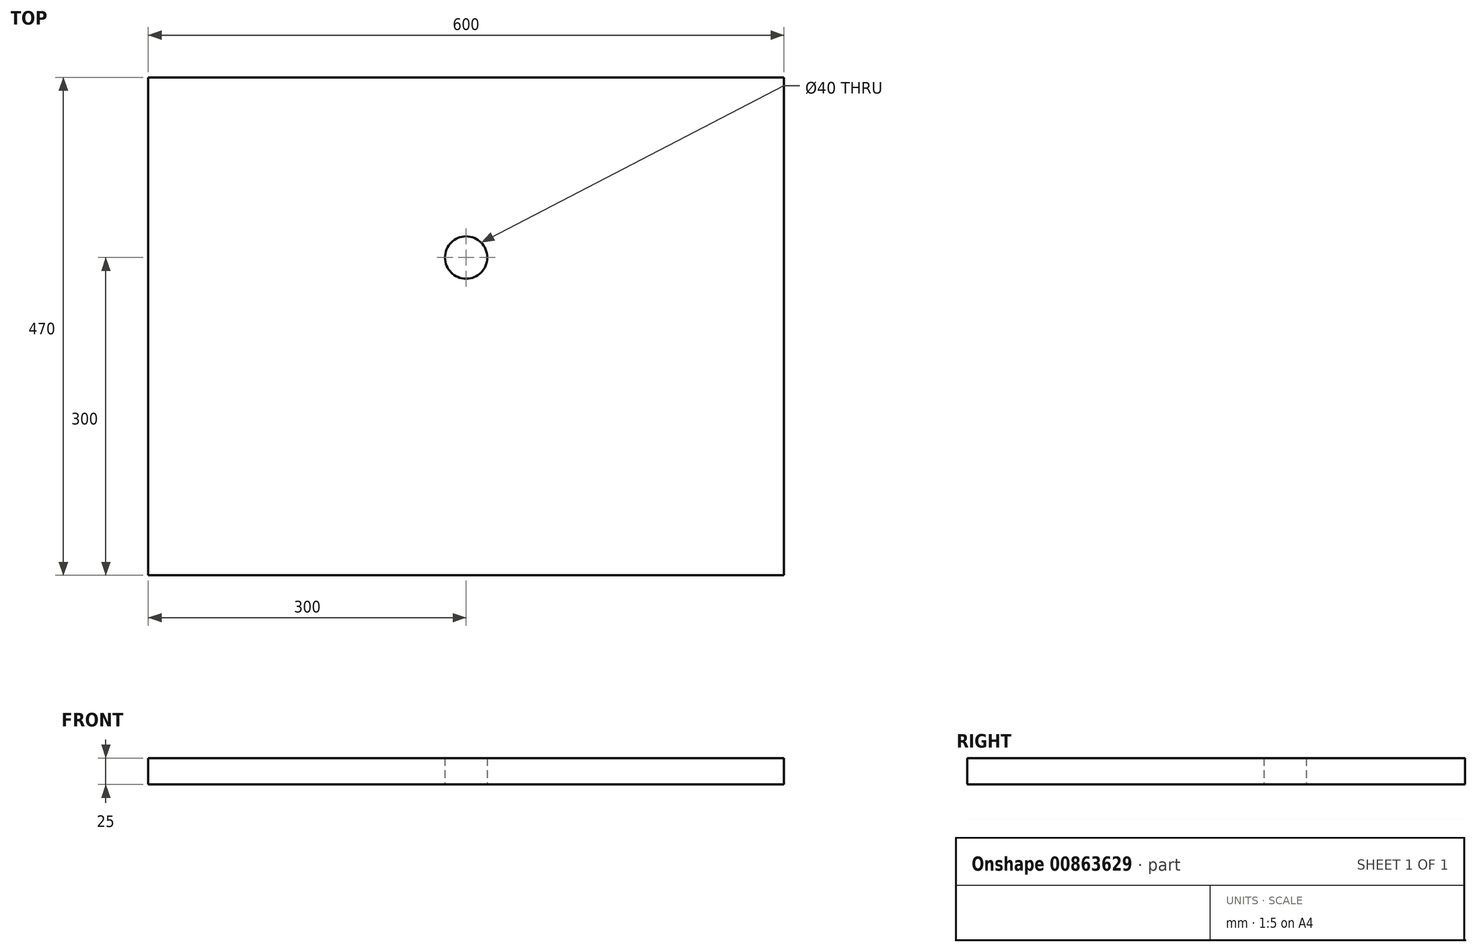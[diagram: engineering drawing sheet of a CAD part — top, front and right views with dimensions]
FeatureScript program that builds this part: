
annotation { "Feature Type Name" : "Feature", "Feature Type Description" : "" }
export const myFeature = defineFeature(function(context is Context, id is Id, definition is map)
    precondition{}
    {
        {
            var Q0;
            Q0=qCreatedBy(makeId("Top.planeOp"),FACE);
            var sketch = newSketch(context, id + "F0", { "sketchPlane" : qUnion([Q0])});
            skLineSegment(sketch, "E0.bottom", {"start": v(300, -235) * mm, "end": v(-300, -235) * mm});
            skLineSegment(sketch, "E0.top", {"start": v(300, 235) * mm, "end": v(-300, 235) * mm});
            skLineSegment(sketch, "E0.left", {"start": v(300, -235) * mm, "end": v(300, 235) * mm});
            skLineSegment(sketch, "E0.right", {"start": v(-300, -235) * mm, "end": v(-300, 235) * mm});
            skPoint(sketch, "E0.middle", {"position": v(0, 0) * mm});
            skCircle(sketch, "E1", {"center": v(0, 65) * mm, "radius": 20 * mm});
            skPoint(sketch, "E1.centerSnap0", {"position": v(0, 235) * mm});
            skSolve(sketch);
        }
        {
            var Q0;
            Q0 = qSketchRegion(id + "F0", true);
            extrude(context, id + "F1", {"entities" : qUnion([Q0]), "depth" : 25 * mm, "offsetDistance" : 25 * mm});
        }
    });
